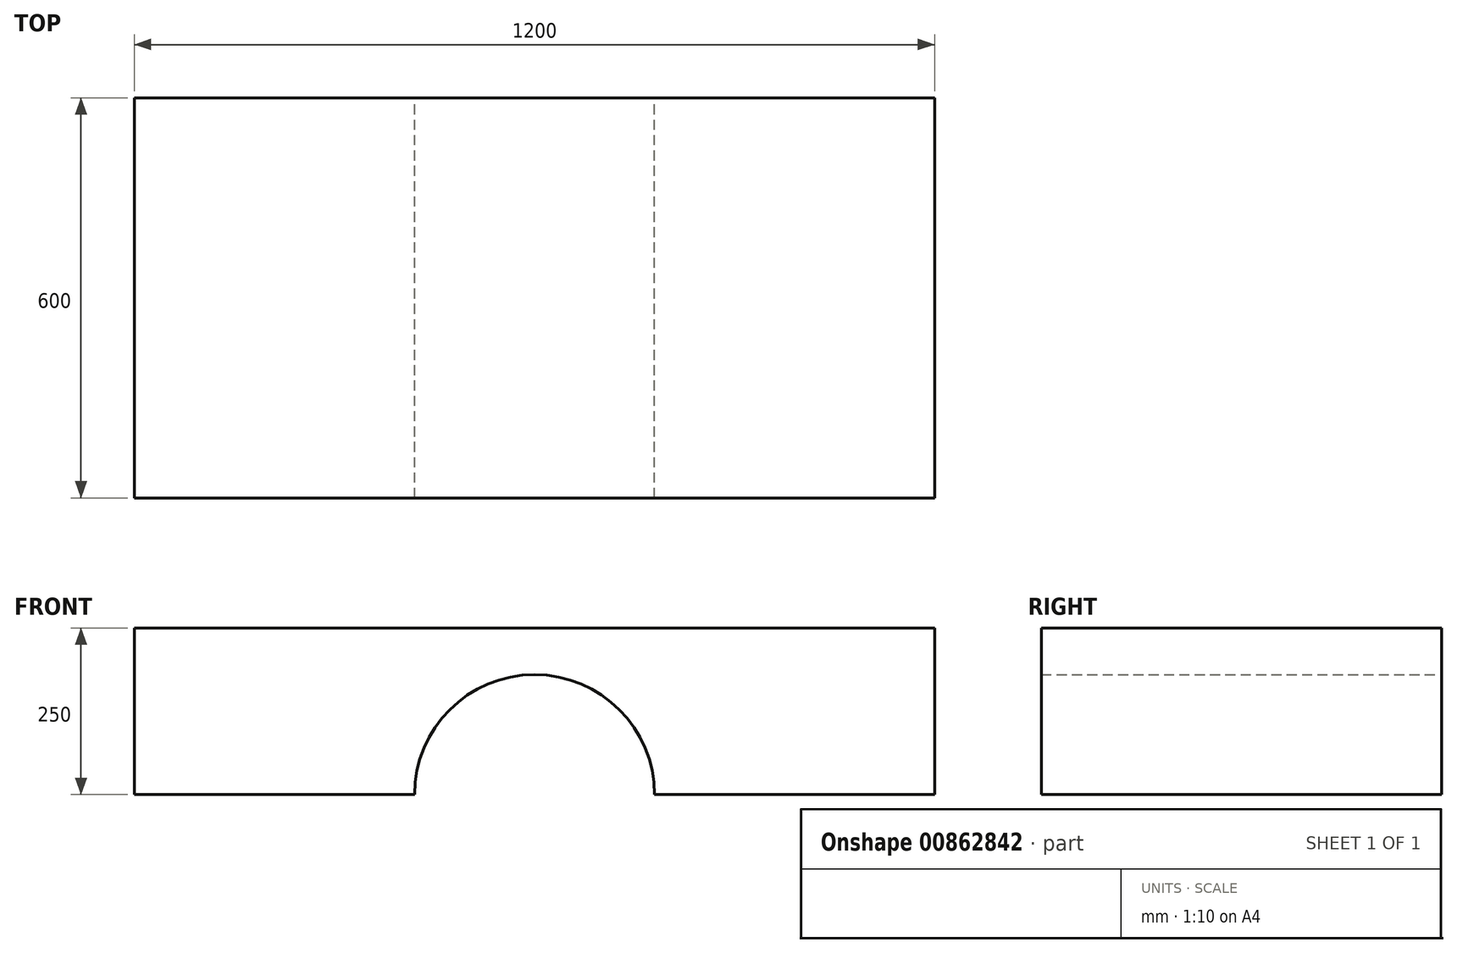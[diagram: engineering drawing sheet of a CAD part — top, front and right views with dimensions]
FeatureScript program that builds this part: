
annotation { "Feature Type Name" : "Feature", "Feature Type Description" : "" }
export const myFeature = defineFeature(function(context is Context, id is Id, definition is map)
    precondition{}
    {
        {
            var Q0;
            Q0=qCreatedBy(makeId("Front.planeOp"),FACE);
            var sketch = newSketch(context, id + "F0", { "sketchPlane" : qUnion([Q0])});
            skLineSegment(sketch, "E0.bottom", {"start": v(600, 125) * mm, "end": v(-600, 125) * mm});
            skLineSegment(sketch, "E0.top", {"start": v(600, -125) * mm, "end": v(180, -125) * mm});
            skLineSegment(sketch, "E0.left", {"start": v(600, 125) * mm, "end": v(600, -125) * mm});
            skLineSegment(sketch, "E0.right", {"start": v(-600, 125) * mm, "end": v(-600, -125) * mm});
            skPoint(sketch, "E0.middle", {"position": v(0, 0) * mm});
            skArc(sketch, "E1", {"start": v(180, -125) * mm, "mid": v(0, 55) * mm, "end": v(-180, -125) * mm});
            skLineSegment(sketch, "E2.trimOffspring", {"start": v(-180, -125) * mm, "end": v(-600, -125) * mm});
            skSolve(sketch);
        }
        {
            var Q0;
            Q0 = qSketchRegion(id + "F0", true);
            extrude(context, id + "F1", {"entities" : qUnion([Q0]), "depth" : 600 * mm, "offsetDistance" : 25 * mm});
        }
        {
            var Q0;
            Q0 = qSketchRegion(id + "F0", true);
            extrude(context, id + "F2", {"entities" : qUnion([Q0]), "operationType" : NewBodyOperationType.ADD, "depth" : 500 * mm, "offsetDistance" : 25 * mm});
        }
    });
